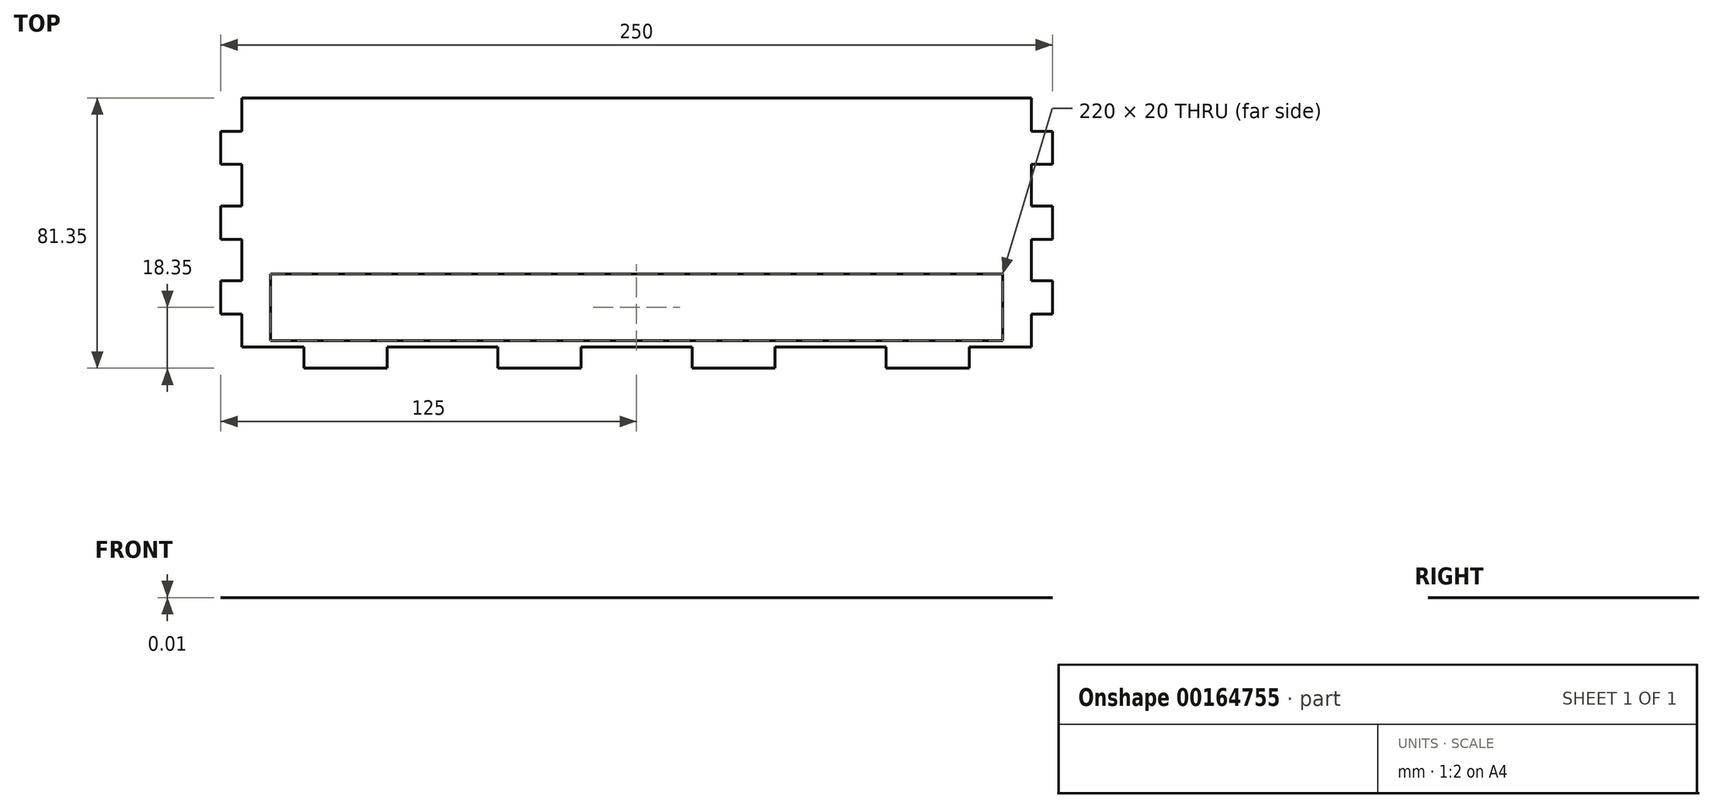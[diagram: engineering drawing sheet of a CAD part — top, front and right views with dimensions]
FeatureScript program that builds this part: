
annotation { "Feature Type Name" : "Feature", "Feature Type Description" : "" }
export const myFeature = defineFeature(function(context is Context, id is Id, definition is map)
    precondition{}
    {
        {
            var Q0;
            Q0=qCreatedBy(makeId("Top.planeOp"),FACE);
            var sketch = newSketch(context, id + "F0", { "sketchPlane" : qUnion([Q0])});
            skLineSegment(sketch, "E0.bottom", {"start": v(-125, 37.5) * mm, "end": v(125, 37.5) * mm});
            skLineSegment(sketch, "E0.top", {"start": v(-125, -37.5) * mm, "end": v(125, -37.5) * mm});
            skLineSegment(sketch, "E0.left", {"start": v(-125, 37.5) * mm, "end": v(-125, -37.5) * mm});
            skLineSegment(sketch, "E0.right", {"start": v(125, 37.5) * mm, "end": v(125, -37.5) * mm});
            skPoint(sketch, "E0.middle", {"position": v(0, 0) * mm});
            skSolve(sketch);
        }
        {
            var Q0;
            Q0=qSketchRegion(id+"F0",true);
            extrude(context, id + "F1", {"entities" : qUnion([Q0]), "depth" : 1 / 101.6 * mm});
        }
        {
            var Q0;
            Q0=makeQuery(id+"F1.opExtrude","CAP_FACE",FACE,{"disambiguationData":[OSD([sQuery(id+"F0.wireOp",EDGE,"E0.bottom"),sQuery(id+"F0.wireOp",EDGE,"E0.top"),sQuery(id+"F0.wireOp",EDGE,"E0.left"),sQuery(id+"F0.wireOp",EDGE,"E0.right")])],"isStart":false});
            var sketch = newSketch(context, id + "F2", { "sketchPlane" : qUnion([Q0])});
            skLineSegment(sketch, "E1.bottom", {"start": v(-100, -37.5) * mm, "end": v(-75, -37.5) * mm});
            skLineSegment(sketch, "E1.top", {"start": v(-100, -43.85) * mm, "end": v(-75, -43.85) * mm});
            skLineSegment(sketch, "E1.left", {"start": v(-100, -37.5) * mm, "end": v(-100, -43.85) * mm});
            skLineSegment(sketch, "E1.right", {"start": v(-75, -37.5) * mm, "end": v(-75, -43.85) * mm});
            skLineSegment(sketch, "E2.1.0.0", {"start": v(-41.67, -37.5) * mm, "end": v(-16.67, -37.5) * mm});
            skLineSegment(sketch, "E2.1.0.1", {"start": v(-41.67, -43.85) * mm, "end": v(-16.67, -43.85) * mm});
            skLineSegment(sketch, "E2.1.0.2", {"start": v(-41.67, -37.5) * mm, "end": v(-41.67, -43.85) * mm});
            skLineSegment(sketch, "E2.1.0.3", {"start": v(-16.67, -37.5) * mm, "end": v(-16.67, -43.85) * mm});
            skLineSegment(sketch, "E2.2.0.0", {"start": v(16.66, -37.5) * mm, "end": v(41.66, -37.5) * mm});
            skLineSegment(sketch, "E2.2.0.1", {"start": v(16.66, -43.85) * mm, "end": v(41.66, -43.85) * mm});
            skLineSegment(sketch, "E2.2.0.2", {"start": v(16.66, -37.5) * mm, "end": v(16.66, -43.85) * mm});
            skLineSegment(sketch, "E2.2.0.3", {"start": v(41.66, -37.5) * mm, "end": v(41.66, -43.85) * mm});
            skLineSegment(sketch, "E2.3.0.0", {"start": v(75, -37.5) * mm, "end": v(100, -37.5) * mm});
            skLineSegment(sketch, "E2.3.0.1", {"start": v(75, -43.85) * mm, "end": v(100, -43.85) * mm});
            skLineSegment(sketch, "E2.3.0.2", {"start": v(75, -37.5) * mm, "end": v(75, -43.85) * mm});
            skLineSegment(sketch, "E2.3.0.3", {"start": v(100, -37.5) * mm, "end": v(100, -43.85) * mm});
            skLineSegment(sketch, "E2.direction1", {"start": v(-100, -43.85) * mm, "end": v(-41.67, -43.85) * mm, "construction": true});
            skSolve(sketch);
        }
        {
            var Q0;
            Q0 = qSketchRegion(id + "F2", true);
            var Q1;
            Q1=makeQuery(id+"F1.opExtrude","CAP_FACE",FACE,{"disambiguationData":[OSD([sQuery(id+"F0.wireOp",EDGE,"E0.bottom"),sQuery(id+"F0.wireOp",EDGE,"E0.top"),sQuery(id+"F0.wireOp",EDGE,"E0.left"),sQuery(id+"F0.wireOp",EDGE,"E0.right")])],"isStart":true});
            extrude(context, id + "F3", {"entities" : qUnion([Q0]), "operationType" : NewBodyOperationType.ADD, "endBound" : BoundingType.UP_TO_SURFACE, "oppositeDirection" : true, "endBoundEntityFace" : qUnion([Q1]), "depth" : 25 * mm});
        }
        {
            var Q0;
            Q0=makeQuery(id+"F3.boolean.opBoolean","MERGE",FACE,{"derivedFrom":[makeQuery(id+"F1.opExtrude","CAP_FACE",FACE,{"disambiguationData":[OSD([sQuery(id+"F0.wireOp",EDGE,"E0.bottom"),sQuery(id+"F0.wireOp",EDGE,"E0.top"),sQuery(id+"F0.wireOp",EDGE,"E0.left"),sQuery(id+"F0.wireOp",EDGE,"E0.right")])],"isStart":false}),makeQuery(id+"F3.opExtrude","CAP_FACE",FACE,{"disambiguationData":[OSD([sQuery(id+"F2.wireOp",EDGE,"E1.bottom"),sQuery(id+"F2.wireOp",EDGE,"E1.top"),sQuery(id+"F2.wireOp",EDGE,"E1.left"),sQuery(id+"F2.wireOp",EDGE,"E1.right")])],"isStart":true}),makeQuery(id+"F3.opExtrude","CAP_FACE",FACE,{"disambiguationData":[OSD([sQuery(id+"F2.wireOp",EDGE,"E2.1.0.0"),sQuery(id+"F2.wireOp",EDGE,"E2.1.0.1"),sQuery(id+"F2.wireOp",EDGE,"E2.1.0.2"),sQuery(id+"F2.wireOp",EDGE,"E2.1.0.3")])],"isStart":true}),makeQuery(id+"F3.opExtrude","CAP_FACE",FACE,{"disambiguationData":[OSD([sQuery(id+"F2.wireOp",EDGE,"E2.2.0.0"),sQuery(id+"F2.wireOp",EDGE,"E2.2.0.1"),sQuery(id+"F2.wireOp",EDGE,"E2.2.0.2"),sQuery(id+"F2.wireOp",EDGE,"E2.2.0.3")])],"isStart":true}),makeQuery(id+"F3.opExtrude","CAP_FACE",FACE,{"disambiguationData":[OSD([sQuery(id+"F2.wireOp",EDGE,"E2.3.0.0"),sQuery(id+"F2.wireOp",EDGE,"E2.3.0.1"),sQuery(id+"F2.wireOp",EDGE,"E2.3.0.2"),sQuery(id+"F2.wireOp",EDGE,"E2.3.0.3")])],"isStart":true})]});
            var sketch = newSketch(context, id + "F4", { "sketchPlane" : qUnion([Q0])});
            skLineSegment(sketch, "E3.bottom", {"start": v(-110, -15.5) * mm, "end": v(110, -15.5) * mm});
            skLineSegment(sketch, "E3.top", {"start": v(-110, -35.5) * mm, "end": v(110, -35.5) * mm});
            skLineSegment(sketch, "E3.left", {"start": v(-110, -15.5) * mm, "end": v(-110, -35.5) * mm});
            skLineSegment(sketch, "E3.right", {"start": v(110, -15.5) * mm, "end": v(110, -35.5) * mm});
            skLineSegment(sketch, "E4", {"start": v(0, -15.5) * mm, "end": v(0, 0) * mm, "construction": true});
            skSolve(sketch);
        }
        {
            var Q0;
            Q0 = qSketchRegion(id + "F4", true);
            extrude(context, id + "F5", {"entities" : qUnion([Q0]), "operationType" : NewBodyOperationType.REMOVE, "oppositeDirection" : true, "depth" : 25 * mm});
        }
        {
            var Q0;
            Q0=makeQuery(id+"F3.boolean.opBoolean","MERGE",FACE,{"derivedFrom":[makeQuery(id+"F1.opExtrude","CAP_FACE",FACE,{"disambiguationData":[OSD([sQuery(id+"F0.wireOp",EDGE,"E0.bottom"),sQuery(id+"F0.wireOp",EDGE,"E0.top"),sQuery(id+"F0.wireOp",EDGE,"E0.left"),sQuery(id+"F0.wireOp",EDGE,"E0.right")])],"isStart":false}),makeQuery(id+"F3.opExtrude","CAP_FACE",FACE,{"disambiguationData":[OSD([sQuery(id+"F2.wireOp",EDGE,"E1.bottom"),sQuery(id+"F2.wireOp",EDGE,"E1.top"),sQuery(id+"F2.wireOp",EDGE,"E1.left"),sQuery(id+"F2.wireOp",EDGE,"E1.right")])],"isStart":true}),makeQuery(id+"F3.opExtrude","CAP_FACE",FACE,{"disambiguationData":[OSD([sQuery(id+"F2.wireOp",EDGE,"E2.1.0.0"),sQuery(id+"F2.wireOp",EDGE,"E2.1.0.1"),sQuery(id+"F2.wireOp",EDGE,"E2.1.0.2"),sQuery(id+"F2.wireOp",EDGE,"E2.1.0.3")])],"isStart":true}),makeQuery(id+"F3.opExtrude","CAP_FACE",FACE,{"disambiguationData":[OSD([sQuery(id+"F2.wireOp",EDGE,"E2.2.0.0"),sQuery(id+"F2.wireOp",EDGE,"E2.2.0.1"),sQuery(id+"F2.wireOp",EDGE,"E2.2.0.2"),sQuery(id+"F2.wireOp",EDGE,"E2.2.0.3")])],"isStart":true}),makeQuery(id+"F3.opExtrude","CAP_FACE",FACE,{"disambiguationData":[OSD([sQuery(id+"F2.wireOp",EDGE,"E2.3.0.0"),sQuery(id+"F2.wireOp",EDGE,"E2.3.0.1"),sQuery(id+"F2.wireOp",EDGE,"E2.3.0.2"),sQuery(id+"F2.wireOp",EDGE,"E2.3.0.3")])],"isStart":true})]});
            var sketch = newSketch(context, id + "F6", { "sketchPlane" : qUnion([Q0])});
            skLineSegment(sketch, "E5.bottom", {"start": v(125, 37.5) * mm, "end": v(118.65, 37.5) * mm});
            skLineSegment(sketch, "E5.top", {"start": v(125, 27.5) * mm, "end": v(118.65, 27.5) * mm});
            skLineSegment(sketch, "E5.left", {"start": v(125, 37.5) * mm, "end": v(125, 27.5) * mm});
            skLineSegment(sketch, "E5.right", {"start": v(118.65, 37.5) * mm, "end": v(118.65, 27.5) * mm});
            skLineSegment(sketch, "E6.bottom", {"start": v(125, 17.5) * mm, "end": v(118.65, 17.5) * mm});
            skLineSegment(sketch, "E6.top", {"start": v(125, 5) * mm, "end": v(118.65, 5) * mm});
            skLineSegment(sketch, "E6.left", {"start": v(125, 17.5) * mm, "end": v(125, 5) * mm});
            skLineSegment(sketch, "E6.right", {"start": v(118.65, 17.5) * mm, "end": v(118.65, 5) * mm});
            skLineSegment(sketch, "E7.0.1.0", {"start": v(118.65, -5) * mm, "end": v(118.65, -17.5) * mm});
            skLineSegment(sketch, "E7.0.1.1", {"start": v(125, -5) * mm, "end": v(125, -17.5) * mm});
            skLineSegment(sketch, "E7.0.1.2", {"start": v(125, -5) * mm, "end": v(118.65, -5) * mm});
            skLineSegment(sketch, "E7.0.1.3", {"start": v(125, -17.5) * mm, "end": v(118.65, -17.5) * mm});
            skLineSegment(sketch, "E7.direction1", {"start": v(118.65, 5) * mm, "end": v(0, 5) * mm, "construction": true});
            skLineSegment(sketch, "E7.direction2", {"start": v(118.65, 5) * mm, "end": v(118.65, -17.5) * mm, "construction": true});
            skLineSegment(sketch, "E8.bottom", {"start": v(125, -27.5) * mm, "end": v(118.65, -27.5) * mm});
            skLineSegment(sketch, "E8.top", {"start": v(125, -43.85) * mm, "end": v(118.65, -43.85) * mm});
            skLineSegment(sketch, "E8.left", {"start": v(125, -27.5) * mm, "end": v(125, -43.85) * mm});
            skLineSegment(sketch, "E8.right", {"start": v(118.65, -27.5) * mm, "end": v(118.65, -43.85) * mm});
            skLineSegment(sketch, "E9", {"start": v(0, 5) * mm, "end": v(0, 37.5) * mm, "construction": true});
            skLineSegment(sketch, "E10.MirrorCS", {"start": v(-125, -27.5) * mm, "end": v(-118.65, -27.5) * mm});
            skLineSegment(sketch, "E11.MirrorCS", {"start": v(-125, -43.85) * mm, "end": v(-118.65, -43.85) * mm});
            skLineSegment(sketch, "E12.MirrorCS", {"start": v(-125, 27.5) * mm, "end": v(-118.65, 27.5) * mm});
            skLineSegment(sketch, "E13.MirrorCS", {"start": v(-125, 17.5) * mm, "end": v(-118.65, 17.5) * mm});
            skLineSegment(sketch, "E14.MirrorCS", {"start": v(-125, 5) * mm, "end": v(-118.65, 5) * mm});
            skLineSegment(sketch, "E15.MirrorCS", {"start": v(-125, -17.5) * mm, "end": v(-118.65, -17.5) * mm});
            skLineSegment(sketch, "E16.MirrorCS", {"start": v(-125, -5) * mm, "end": v(-118.65, -5) * mm});
            skLineSegment(sketch, "E17.MirrorCS", {"start": v(-125, 37.5) * mm, "end": v(-118.65, 37.5) * mm});
            skLineSegment(sketch, "E18.MirrorCS", {"start": v(-118.65, -5) * mm, "end": v(-118.65, -17.5) * mm});
            skLineSegment(sketch, "E19.MirrorCS", {"start": v(-118.65, 5) * mm, "end": v(-118.65, -17.5) * mm, "construction": true});
            skLineSegment(sketch, "E20.MirrorCS", {"start": v(-125, 37.5) * mm, "end": v(-125, 27.5) * mm});
            skLineSegment(sketch, "E21.MirrorCS", {"start": v(-118.65, 37.5) * mm, "end": v(-118.65, 27.5) * mm});
            skLineSegment(sketch, "E22.MirrorCS", {"start": v(-125, 17.5) * mm, "end": v(-125, 5) * mm});
            skLineSegment(sketch, "E23.MirrorCS", {"start": v(-118.65, 17.5) * mm, "end": v(-118.65, 5) * mm});
            skLineSegment(sketch, "E24.MirrorCS", {"start": v(-125, -5) * mm, "end": v(-125, -17.5) * mm});
            skLineSegment(sketch, "E25.MirrorCS", {"start": v(-118.65, -27.5) * mm, "end": v(-118.65, -43.85) * mm});
            skLineSegment(sketch, "E26.MirrorCS", {"start": v(-125, -27.5) * mm, "end": v(-125, -43.85) * mm});
            skSolve(sketch);
        }
        {
            var Q0;
            Q0 = qSketchRegion(id + "F6", true);
            var Q1;
            {var subQ0=sQuery(id+"F0.wireOp",EDGE,"E0.right");var subQ1=sQuery(id+"F0.wireOp",EDGE,"E0.left");var subQ2=sQuery(id+"F0.wireOp",EDGE,"E0.top");var subQ3=sQuery(id+"F0.wireOp",EDGE,"E0.bottom");Q1=makeQuery(id+"F3.boolean.opBoolean","MERGE",FACE,{"derivedFrom":[makeQuery(id+"F1.opExtrude","CAP_FACE",FACE,{"disambiguationData":[OSD([subQ3,subQ2,subQ1,subQ0])],"isStart":true}),makeQuery(id+"F3.opExtrude","CAP_FACE",FACE,{"disambiguationData":[OSD([subQ3,subQ2,subQ1,subQ0]),ownerDisambiguation([makeQuery(id+"F3.opExtrude","SWEPT_BODY",BODY,{"disambiguationData":[OSD([sQuery(id+"F2.wireOp",EDGE,"E1.bottom"),sQuery(id+"F2.wireOp",EDGE,"E1.top"),sQuery(id+"F2.wireOp",EDGE,"E1.left"),sQuery(id+"F2.wireOp",EDGE,"E1.right")])]})])],"isStart":false}),makeQuery(id+"F3.opExtrude","CAP_FACE",FACE,{"disambiguationData":[OSD([subQ3,subQ2,subQ1,subQ0]),ownerDisambiguation([makeQuery(id+"F3.opExtrude","SWEPT_BODY",BODY,{"disambiguationData":[OSD([sQuery(id+"F2.wireOp",EDGE,"E2.1.0.0"),sQuery(id+"F2.wireOp",EDGE,"E2.1.0.1"),sQuery(id+"F2.wireOp",EDGE,"E2.1.0.2"),sQuery(id+"F2.wireOp",EDGE,"E2.1.0.3")])]})])],"isStart":false}),makeQuery(id+"F3.opExtrude","CAP_FACE",FACE,{"disambiguationData":[OSD([subQ3,subQ2,subQ1,subQ0]),ownerDisambiguation([makeQuery(id+"F3.opExtrude","SWEPT_BODY",BODY,{"disambiguationData":[OSD([sQuery(id+"F2.wireOp",EDGE,"E2.2.0.0"),sQuery(id+"F2.wireOp",EDGE,"E2.2.0.1"),sQuery(id+"F2.wireOp",EDGE,"E2.2.0.2"),sQuery(id+"F2.wireOp",EDGE,"E2.2.0.3")])]})])],"isStart":false}),makeQuery(id+"F3.opExtrude","CAP_FACE",FACE,{"disambiguationData":[OSD([subQ3,subQ2,subQ1,subQ0]),ownerDisambiguation([makeQuery(id+"F3.opExtrude","SWEPT_BODY",BODY,{"disambiguationData":[OSD([sQuery(id+"F2.wireOp",EDGE,"E2.3.0.0"),sQuery(id+"F2.wireOp",EDGE,"E2.3.0.1"),sQuery(id+"F2.wireOp",EDGE,"E2.3.0.2"),sQuery(id+"F2.wireOp",EDGE,"E2.3.0.3")])]})])],"isStart":false})]});}
            extrude(context, id + "F7", {"entities" : qUnion([Q0]), "operationType" : NewBodyOperationType.REMOVE, "endBound" : BoundingType.UP_TO_SURFACE, "oppositeDirection" : true, "endBoundEntityFace" : qUnion([Q1]), "depth" : 25 * mm});
        }
    });
